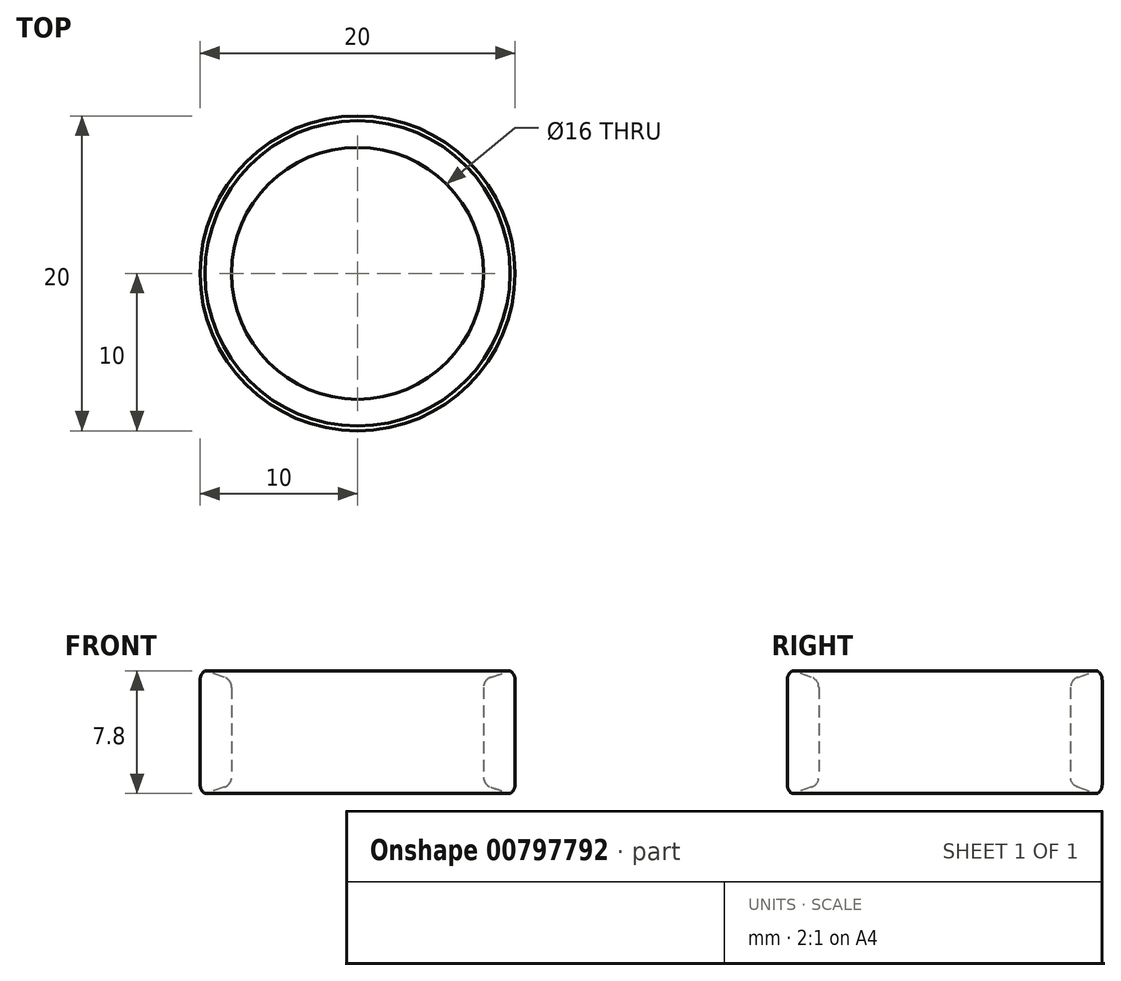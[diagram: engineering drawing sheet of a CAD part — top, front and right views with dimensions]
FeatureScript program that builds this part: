
annotation { "Feature Type Name" : "Feature", "Feature Type Description" : "" }
export const myFeature = defineFeature(function(context is Context, id is Id, definition is map)
    precondition{}
    {
        {
            assignVariable(context, id + "F0", {"name" : "wandstaerke", "anyValue" : 2});
        }
        {
            assignVariable(context, id + "F1", {"name" : "breite", "anyValue" : 8});
        }
        {
            var Q0;
            Q0=qCreatedBy(makeId("Top.planeOp"),FACE);
            var sketch = newSketch(context, id + "F2", { "sketchPlane" : qUnion([Q0])});
            skCircle(sketch, "E0", {"center": v(0, 0) * mm, "radius": 8 * mm});
            skCircle(sketch, "E1", {"center": v(0, 0) * mm, "radius": 10 * mm});
            skSolve(sketch);
        }
        {
            var Q0;
            Q0=makeQuery(id+"F2.imprint","IMPRINT",FACE,{"disambiguationData":[TD([[makeQuery(id+"F2.imprint","IMPRINT",EDGE,{"derivedFrom":sQuery(id+"F2.wireOp",EDGE,"E0")}),-1.0]])]});
            extrude(context, id + "F3", {"entities" : qUnion([Q0]), "depth" : (getVariable(context, 'breite')) * mm, "offsetDistance" : 25 * mm});
        }
        {
            var Q0;
            Q0=makeQuery(id+"F3.opExtrude","CAP_EDGE",EDGE,{"disambiguationData":[OSD([sQuery(id+"F2.wireOp",EDGE,"E1")])],"isStart":false});
            var Q1;
            Q1=makeQuery(id+"F3.opExtrude","CAP_EDGE",EDGE,{"disambiguationData":[OSD([sQuery(id+"F2.wireOp",EDGE,"E1")])],"isStart":true});
            fillet(context, id + "F4", {"entities" : qUnion([Q0, Q1]), "radius" : (getVariable(context, 'wandstaerke') / 3) * mm, "tangentPropagation" : true, "allowEdgeOverflow" : false});
        }
        {
            var Q0;
            Q0=makeQuery(id+"F3.opExtrude","CAP_EDGE",EDGE,{"disambiguationData":[OSD([sQuery(id+"F2.wireOp",EDGE,"E0")])],"isStart":true});
            var Q1;
            Q1=makeQuery(id+"F3.opExtrude","CAP_EDGE",EDGE,{"disambiguationData":[OSD([sQuery(id+"F2.wireOp",EDGE,"E0")])],"isStart":false});
            chamfer(context, id + "F5", {"entities" : qUnion([Q0, Q1]), "chamferType" : ChamferType.TWO_OFFSETS, "width1" : (getVariable(context, 'wandstaerke')) * mm, "oppositeDirection" : false, "width2" : (getVariable(context, 'wandstaerke') / 3) * mm, "tangentPropagation" : true});
        }
        {
            var Q0;
            {var subQ0=sQuery(id+"F2.wireOp",EDGE,"E0");Q0=makeQuery(id+"F5.opChamfer","BLEND_EDGE",EDGE,{"blendedFrom":[makeQuery(id+"F3.opExtrude","CAP_EDGE",EDGE,{"disambiguationData":[OSD([subQ0])],"isStart":false}),makeQuery(id+"F3.opExtrude","SWEPT_FACE",FACE,{"disambiguationData":[OSD([subQ0])]})],"blendedInto":[makeQuery(id+"F3.opExtrude","SWEPT_FACE",FACE,{"disambiguationData":[OSD([subQ0])]})]});}
            var Q1;
            {var subQ0=sQuery(id+"F2.wireOp",EDGE,"E0");Q1=makeQuery(id+"F5.opChamfer","BLEND_EDGE",EDGE,{"blendedFrom":[makeQuery(id+"F3.opExtrude","CAP_EDGE",EDGE,{"disambiguationData":[OSD([subQ0])],"isStart":true}),makeQuery(id+"F3.opExtrude","SWEPT_FACE",FACE,{"disambiguationData":[OSD([subQ0])]})],"blendedInto":[makeQuery(id+"F3.opExtrude","SWEPT_FACE",FACE,{"disambiguationData":[OSD([subQ0])]})]});}
            fillet(context, id + "F6", {"entities" : qUnion([Q0, Q1]), "radius" : (getVariable(context, 'wandstaerke') / 3) * mm, "tangentPropagation" : true, "allowEdgeOverflow" : false});
        }
    });
